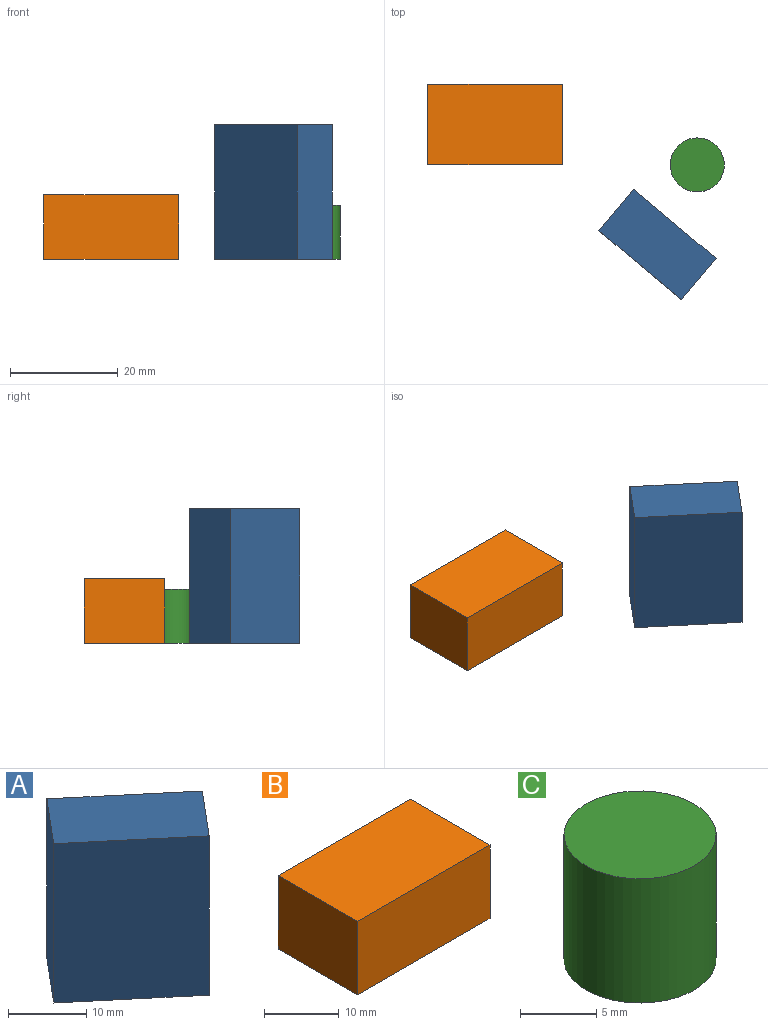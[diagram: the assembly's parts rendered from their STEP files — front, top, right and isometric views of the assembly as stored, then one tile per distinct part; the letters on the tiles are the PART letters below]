
ASSEMBLY  parts=3 mates=2
PART A: 6 faces, bbox 21.7x20.5x25 mm
  f0: plane 25x15.32mm, normal (0.64,0.77,0), area 500mm2, adj f1,f3,f4,f5
  f1: plane 25x7.66mm, normal (-0.77,0.64,0), area 250mm2, adj f0,f2,f4,f5
  f2: plane 25x15.32mm, normal (-0.64,-0.77,0), area 500mm2, adj f1,f3,f4,f5
  f3: plane 25x7.66mm, normal (0.77,-0.64,0), area 250mm2, adj f0,f2,f4,f5
  f4: plane 21.75x20.52mm, normal (0,0,1), area 200mm2, adj f0,f1,f2,f3
  f5: plane 21.75x20.52mm, normal (0,0,-1), area 200mm2, adj f0,f1,f2,f3
PART B: 6 faces, bbox 25x15x12 mm
  f0: plane 15x12mm, normal (-1,0,0), area 180mm2, adj f1,f3,f4,f5
  f1: plane 25x12mm, normal (0,-1,0), area 300mm2, adj f0,f2,f4,f5
  f2: plane 15x12mm, normal (1,0,0), area 180mm2, adj f1,f3,f4,f5
  f3: plane 25x12mm, normal (0,1,0), area 300mm2, adj f0,f2,f4,f5
  f4: plane 25x15mm, normal (0,0,1), area 375mm2, adj f0,f1,f2,f3
  f5: plane 25x15mm, normal (0,0,-1), area 375mm2, adj f0,f1,f2,f3
PART C: 3 faces, bbox 10x10x10 mm
  f0: cylinder r=5mm len=10mm, axis (0,0,-1), area 314.2mm2, adj f1,f2
  f1: plane 10x10mm, normal (0,0,1), area 78.5mm2, adj f0
  f2: plane 10x10mm, normal (0,0,-1), area 78.5mm2, adj f0
PLACE A rot(axis=(-1,0,0),0deg) t=(0,0,0)mm
PLACE B at identity fixed
PLACE C t=(20,0,0)mm
MATE fastened B.f5 <-> C.f2  axis (0,0,1) through (0,0,0)mm
MATE fastened B.f5 <-> A.f5  axis (0,0,1) through (0,0,0)mm
